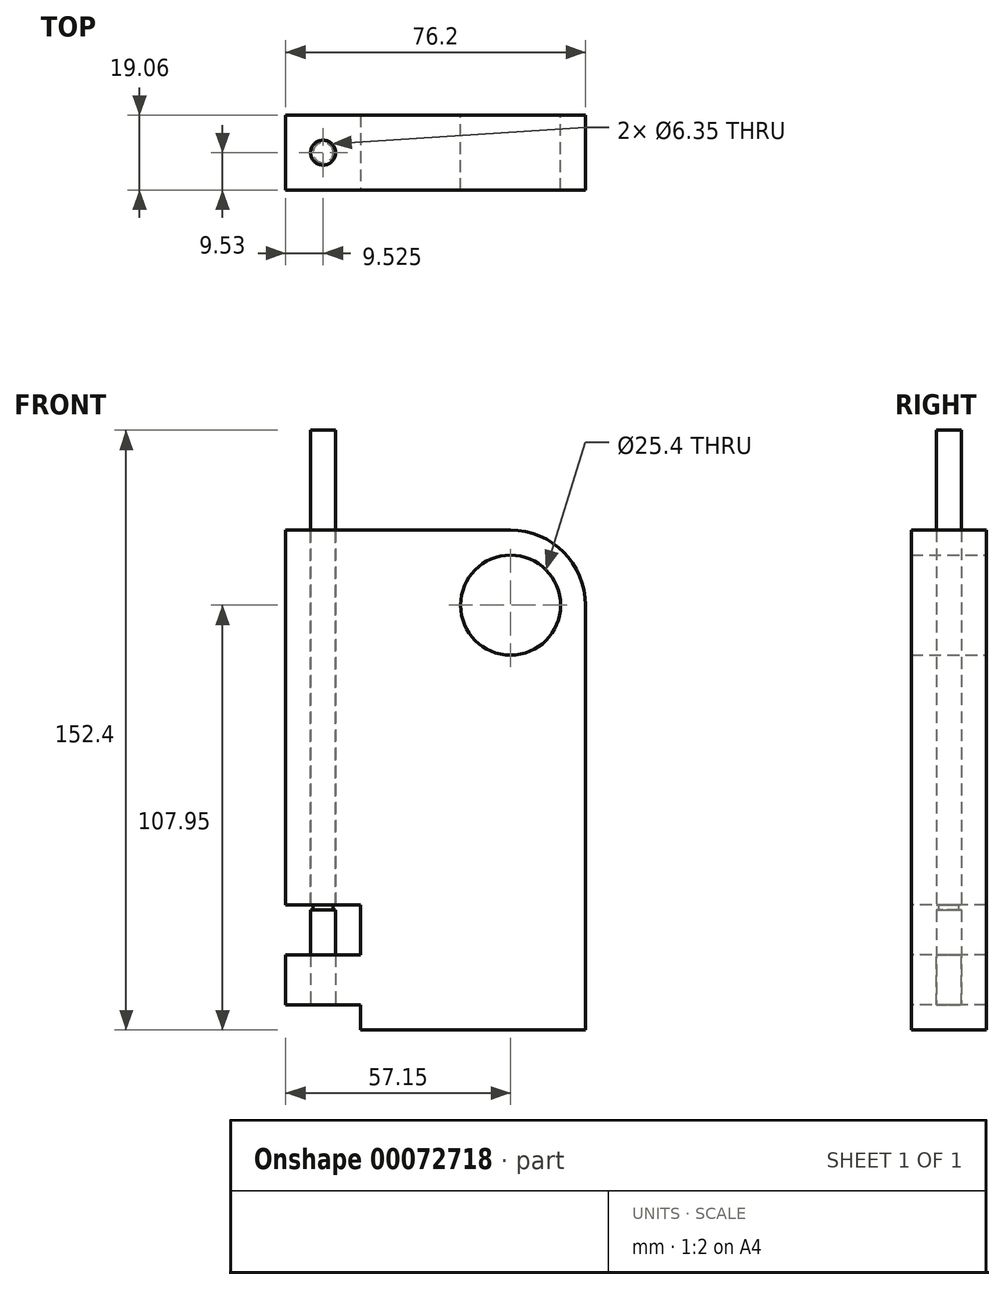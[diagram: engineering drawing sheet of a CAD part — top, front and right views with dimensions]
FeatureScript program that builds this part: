
annotation { "Feature Type Name" : "Feature", "Feature Type Description" : "" }
export const myFeature = defineFeature(function(context is Context, id is Id, definition is map)
    precondition{}
    {
        {
            var Q0;
            Q0=qCreatedBy(makeId("Front.planeOp"),FACE);
            var sketch = newSketch(context, id + "F0", { "sketchPlane" : qUnion([Q0])});
            skLineSegment(sketch, "E0.bottom", {"start": v(0, 127) * mm, "end": v(57.15, 127) * mm});
            skLineSegment(sketch, "E0.top", {"start": v(0, 0) * mm, "end": v(76.2, 0) * mm});
            skLineSegment(sketch, "E0.left", {"start": v(0, 127) * mm, "end": v(0, 0) * mm});
            skLineSegment(sketch, "E0.right", {"start": v(76.2, 107.95) * mm, "end": v(76.2, 0) * mm});
            skPoint(sketch, "E1.visualSharp", {"position": v(76.2, 127) * mm});
            skArc(sketch, "E1.filletArc", {"start": v(76.2, 107.95) * mm, "mid": v(70.62, 121.42) * mm, "end": v(57.15, 127) * mm});
            skCircle(sketch, "E2", {"center": v(57.15, 107.95) * mm, "radius": 12.7 * mm});
            skSolve(sketch);
        }
        {
            var Q0;
            Q0 = qSketchRegion(id + "F0", true);
            extrude(context, id + "F1", {"entities" : qUnion([Q0]), "endBound" : BoundingType.SYMMETRIC, "depth" : 19.05 * mm});
        }
        {
            var Q0;
            Q0=qCreatedBy(makeId("Front.planeOp"),FACE);
            var sketch = newSketch(context, id + "F2", { "sketchPlane" : qUnion([Q0])});
            skLineSegment(sketch, "E3.bottom", {"start": v(0, 0) * mm, "end": v(19.05, 0) * mm});
            skLineSegment(sketch, "E3.top", {"start": v(0, 6.35) * mm, "end": v(19.05, 6.35) * mm});
            skLineSegment(sketch, "E3.left", {"start": v(0, 0) * mm, "end": v(0, 6.35) * mm});
            skLineSegment(sketch, "E3.right", {"start": v(19.05, 0) * mm, "end": v(19.05, 6.35) * mm});
            skPoint(sketch, "E4.firstSnap0", {"position": v(0, 3.17) * mm});
            skPoint(sketch, "E4.oppositeSnap0", {"position": v(19.05, 3.18) * mm});
            skLineSegment(sketch, "E4.bottom", {"start": v(0, 19.05) * mm, "end": v(19.05, 19.05) * mm});
            skLineSegment(sketch, "E4.top", {"start": v(0, 31.75) * mm, "end": v(19.05, 31.75) * mm});
            skLineSegment(sketch, "E4.left", {"start": v(0, 19.05) * mm, "end": v(0, 31.75) * mm});
            skLineSegment(sketch, "E4.right", {"start": v(19.05, 19.05) * mm, "end": v(19.05, 31.75) * mm});
            skSolve(sketch);
        }
        {
            var Q0;
            Q0 = qSketchRegion(id + "F2", true);
            extrude(context, id + "F3", {"entities" : qUnion([Q0]), "operationType" : NewBodyOperationType.REMOVE, "endBound" : BoundingType.THROUGH_ALL, "oppositeDirection" : true, "depth" : 25.4 * mm, "hasSecondDirection" : true, "secondDirectionBound" : SecondDirectionBoundingType.THROUGH_ALL, "secondDirectionOppositeDirection" : false, "secondDirectionDepth" : 25.4 * mm});
        }
        {
            var Q0;
            Q0=makeQuery(id+"F1.opExtrude","SWEPT_FACE",FACE,{"disambiguationData":[OSD([sQuery(id+"F0.wireOp",EDGE,"E0.bottom")])]});
            var sketch = newSketch(context, id + "F4", { "sketchPlane" : qUnion([Q0])});
            skCircle(sketch, "E5", {"center": v(9.52, 0) * mm, "radius": 3.18 * mm});
            skPoint(sketch, "E5.centerSnap0", {"position": v(0, 0) * mm});
            skLineSegment(sketch, "E6", {"start": v(0, 0) * mm, "end": v(9.52, 0) * mm, "construction": true});
            skLineSegment(sketch, "E7", {"start": v(9.52, 0) * mm, "end": v(9.52, 9.53) * mm, "construction": true});
            skSolve(sketch);
        }
        {
            var Q0;
            Q0 = qSketchRegion(id + "F4", true);
            extrude(context, id + "F5", {"entities" : qUnion([Q0]), "operationType" : NewBodyOperationType.REMOVE, "endBound" : BoundingType.THROUGH_ALL, "oppositeDirection" : true, "depth" : 25.4 * mm});
        }
        {
            var Q0;
            Q0 = qSketchRegion(id + "F4", true);
            var Q1;
            Q1=makeQuery(id+"F3.boolean.opBoolean","COPY",FACE,{"derivedFrom":makeQuery(id+"F3.opExtrude","SWEPT_FACE",FACE,{"disambiguationData":[OSD([sQuery(id+"F2.wireOp",EDGE,"E3.top")])]})});
            extrude(context, id + "F6", {"entities" : qUnion([Q0]), "depth" : 25.4 * mm, "hasSecondDirection" : true, "secondDirectionBound" : SecondDirectionBoundingType.UP_TO_SURFACE, "secondDirectionOppositeDirection" : true, "secondDirectionBoundEntityFace" : qUnion([Q1]), "secondDirectionDepth" : 25.4 * mm});
        }
        {
            var Q0;
            Q0=makeQuery(id+"F3.boolean.opBoolean","COPY",FACE,{"derivedFrom":makeQuery(id+"F3.opExtrude","SWEPT_FACE",FACE,{"disambiguationData":[OSD([sQuery(id+"F2.wireOp",EDGE,"E4.top")])]})});
            var sketch = newSketch(context, id + "F7", { "sketchPlane" : qUnion([Q0])});
            skCircle(sketch, "E8", {"center": v(9.52, 0) * mm, "radius": 2.54 * mm});
            skCircle(sketch, "E9.0", {"center": v(9.52, 0) * mm, "radius": 3.18 * mm});
            skSolve(sketch);
        }
        {
            var Q0;
            Q0 = qSketchRegion(id + "F7", true);
            extrude(context, id + "F8", {"entities" : qUnion([Q0]), "operationType" : NewBodyOperationType.REMOVE, "depth" : 1.27 * mm});
        }
    });
